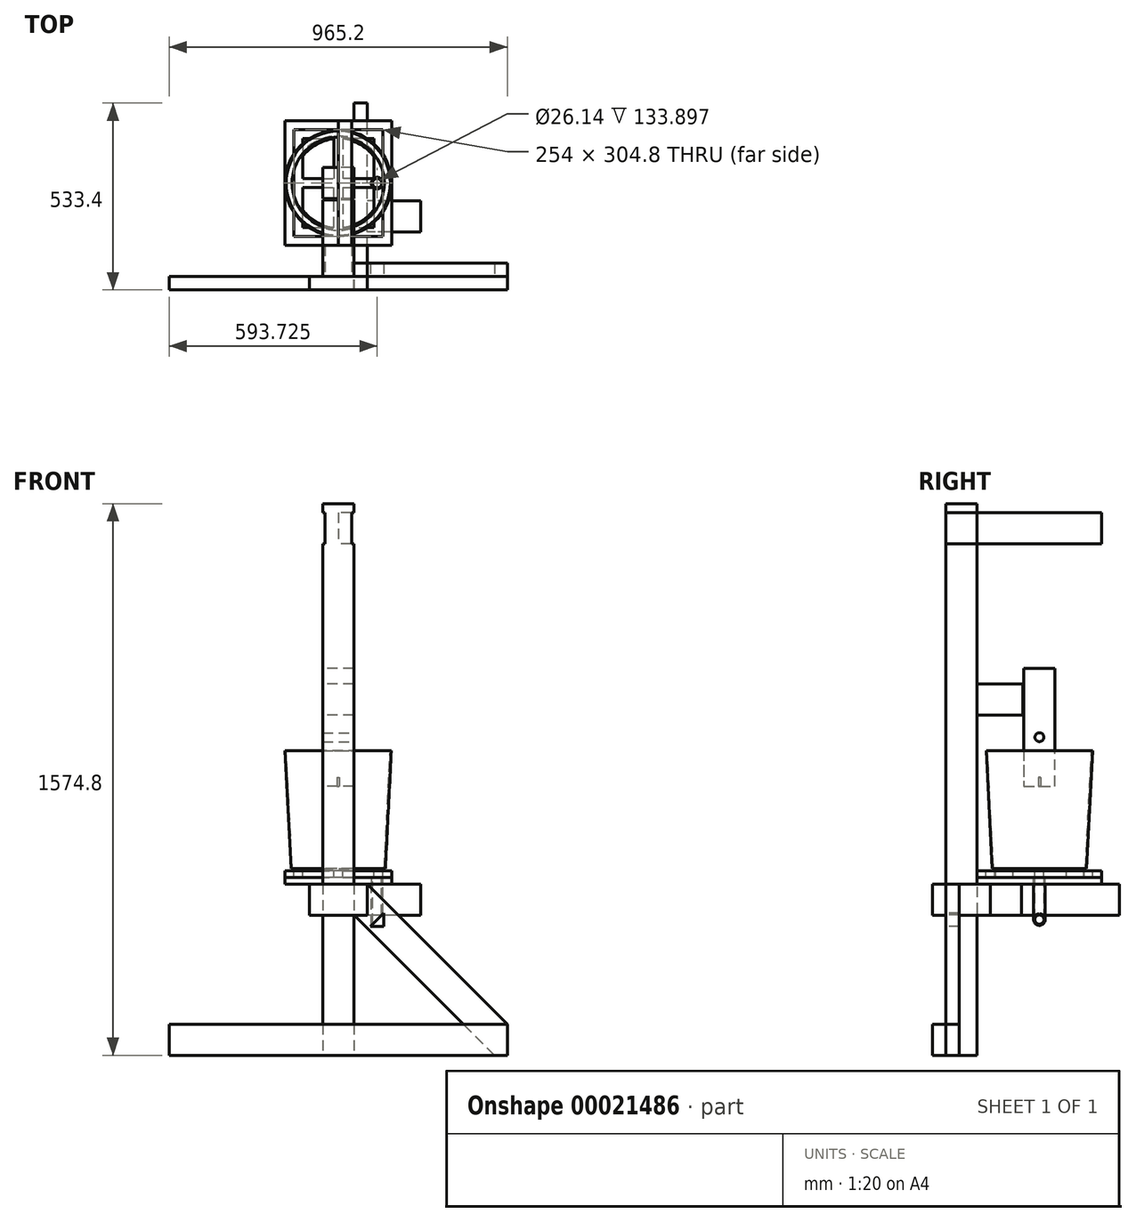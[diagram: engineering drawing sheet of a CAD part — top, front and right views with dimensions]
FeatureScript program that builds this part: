
annotation { "Feature Type Name" : "Feature", "Feature Type Description" : "" }
export const myFeature = defineFeature(function(context is Context, id is Id, definition is map)
    precondition{}
    {
        {
            var Q0;
            Q0=qCreatedBy(makeId("Front.planeOp"),FACE);
            var sketch = newSketch(context, id + "F0", { "sketchPlane" : qUnion([Q0])});
            skLineSegment(sketch, "E0", {"start": v(0, 0) * mm, "end": v(133.35, 0) * mm});
            skLineSegment(sketch, "E1", {"start": v(133.35, 0) * mm, "end": v(151.6, 361.95) * mm});
            skLineSegment(sketch, "E2", {"start": v(151.6, 361.95) * mm, "end": v(0, 361.95) * mm});
            skLineSegment(sketch, "E3", {"start": v(0, 361.95) * mm, "end": v(0, 0) * mm});
            skLineSegment(sketch, "E4", {"start": v(0, 0) * mm, "end": v(0, -74.22) * mm, "construction": true});
            skSolve(sketch);
        }
        {
            var Q0;
            Q0=qSketchRegion(id+"F0",true);
            var Q1;
            Q1=sQuery(id+"F0.wireOp",EDGE,"E4");
            revolve(context, id + "F1", {"entities" : qUnion([Q0]), "axis" : qUnion([Q1]), "revolveType" : RevolveType.FULL});
        }
        {
            var Q0;
            Q0=makeQuery(id+"F1.opRevolve","SWEPT_FACE",FACE,{"disambiguationData":[OSD([sQuery(id+"F0.wireOp",EDGE,"E2")])]});
            shell(context, id + "F2", {"entities" : qUnion([Q0]), "thickness" : 3.17 * mm});
        }
        {
            var Q0;
            Q0=qCreatedBy(makeId("Front.planeOp"),FACE);
            var sketch = newSketch(context, id + "F3", { "sketchPlane" : qUnion([Q0])});
            skLineSegment(sketch, "E5.bottom", {"start": v(-144.72, 25.4) * mm, "end": v(147.3, 25.4) * mm});
            skLineSegment(sketch, "E5.top", {"start": v(-144.72, -21.83) * mm, "end": v(147.3, -21.83) * mm});
            skLineSegment(sketch, "E5.left", {"start": v(-144.72, 25.4) * mm, "end": v(-144.72, -21.83) * mm});
            skLineSegment(sketch, "E5.right", {"start": v(147.3, 25.4) * mm, "end": v(147.3, -21.83) * mm});
            skSolve(sketch);
        }
        {
            var Q0;
            Q0=qSketchRegion(id+"F3",true);
            extrude(context, id + "F4", {"entities" : qUnion([Q0]), "operationType" : NewBodyOperationType.REMOVE, "endBound" : BoundingType.THROUGH_ALL, "depth" : 25.4 * mm, "hasSecondDirection" : true, "secondDirectionBound" : BoundingType.THROUGH_ALL, "secondDirectionOppositeDirection" : true, "secondDirectionDepth" : 25.4 * mm});
        }
        {
            var Q0;
            Q0=qCreatedBy(makeId("Top.planeOp"),FACE);
            var sketch = newSketch(context, id + "F5", { "sketchPlane" : qUnion([Q0])});
            skCircle(sketch, "E6", {"center": v(0, 0) * mm, "radius": 127 * mm});
            skSolve(sketch);
        }
        {
            var Q0;
            Q0=qSketchRegion(id+"F5",true);
            extrude(context, id + "F6", {"entities" : qUnion([Q0]), "depth" : 19.05 * mm});
        }
        {
            var Q0;
            Q0=qCreatedBy(makeId("Top.planeOp"),FACE);
            var sketch = newSketch(context, id + "F7", { "sketchPlane" : qUnion([Q0])});
            skLineSegment(sketch, "E7.rect.bottom", {"start": v(152.4, -177.8) * mm, "end": v(-152.4, -177.8) * mm});
            skLineSegment(sketch, "E7.rect.top", {"start": v(152.4, 177.8) * mm, "end": v(-152.4, 177.8) * mm});
            skLineSegment(sketch, "E7.rect.left", {"start": v(152.4, -177.8) * mm, "end": v(152.4, 177.8) * mm});
            skLineSegment(sketch, "E7.rect.right", {"start": v(-152.4, -177.8) * mm, "end": v(-152.4, 177.8) * mm});
            skPoint(sketch, "E7.rect.middle", {"position": v(0, 0) * mm});
            skCircle(sketch, "E8", {"center": v(111.13, 0) * mm, "radius": 15.88 * mm});
            skSolve(sketch);
        }
        {
            var Q0;
            Q0=qSketchRegion(id+"F7",true);
            extrude(context, id + "F8", {"entities" : qUnion([Q0]), "depth" : 19.05 * mm});
        }
        {
            var Q0;
            Q0=makeQuery(id+"F8.opExtrude","CAP_FACE",FACE,{"disambiguationData":[OSD([sQuery(id+"F7.wireOp",EDGE,"E7.rect.bottom"),sQuery(id+"F7.wireOp",EDGE,"E7.rect.top"),sQuery(id+"F7.wireOp",EDGE,"E7.rect.left"),sQuery(id+"F7.wireOp",EDGE,"E7.rect.right")])],"isStart":true});
            extrude(context, id + "F9", {"entities" : qUnion([Q0]), "depth" : 19.05 * mm});
        }
        {
            var Q0;
            Q0=makeQuery(id+"F8.opExtrude","CAP_FACE",FACE,{"disambiguationData":[OSD([sQuery(id+"F7.wireOp",EDGE,"E7.rect.bottom"),sQuery(id+"F7.wireOp",EDGE,"E7.rect.top"),sQuery(id+"F7.wireOp",EDGE,"E7.rect.left"),sQuery(id+"F7.wireOp",EDGE,"E7.rect.right")])],"isStart":false});
            var sketch = newSketch(context, id + "F10", { "sketchPlane" : qUnion([Q0])});
            skLineSegment(sketch, "E9.rect.bottom", {"start": v(127, 152.4) * mm, "end": v(-127, 152.4) * mm});
            skLineSegment(sketch, "E9.rect.top", {"start": v(127, -152.4) * mm, "end": v(-127, -152.4) * mm});
            skLineSegment(sketch, "E9.rect.left", {"start": v(127, 152.4) * mm, "end": v(127, -152.4) * mm});
            skLineSegment(sketch, "E9.rect.right", {"start": v(-127, 152.4) * mm, "end": v(-127, -152.4) * mm});
            skLineSegment(sketch, "E10.bottom", {"start": v(-101.6, 127) * mm, "end": v(-12.7, 127) * mm});
            skLineSegment(sketch, "E10.top", {"start": v(-101.6, 12.7) * mm, "end": v(-12.7, 12.7) * mm});
            skLineSegment(sketch, "E10.left", {"start": v(-101.6, 127) * mm, "end": v(-101.6, 12.7) * mm});
            skLineSegment(sketch, "E10.right", {"start": v(-12.7, 127) * mm, "end": v(-12.7, 12.7) * mm});
            skLineSegment(sketch, "E11.bottom", {"start": v(101.6, 127) * mm, "end": v(12.7, 127) * mm});
            skLineSegment(sketch, "E11.top", {"start": v(101.6, 12.7) * mm, "end": v(12.7, 12.7) * mm});
            skLineSegment(sketch, "E11.left", {"start": v(101.6, 127) * mm, "end": v(101.6, 12.7) * mm});
            skLineSegment(sketch, "E11.right", {"start": v(12.7, 127) * mm, "end": v(12.7, 12.7) * mm});
            skLineSegment(sketch, "E12.bottom", {"start": v(-101.6, -127) * mm, "end": v(-12.7, -127) * mm});
            skLineSegment(sketch, "E12.top", {"start": v(-101.6, -12.7) * mm, "end": v(-12.7, -12.7) * mm});
            skLineSegment(sketch, "E12.left", {"start": v(-101.6, -127) * mm, "end": v(-101.6, -12.7) * mm});
            skLineSegment(sketch, "E12.right", {"start": v(-12.7, -127) * mm, "end": v(-12.7, -12.7) * mm});
            skLineSegment(sketch, "E13.bottom", {"start": v(12.7, -12.7) * mm, "end": v(101.6, -12.7) * mm});
            skLineSegment(sketch, "E13.top", {"start": v(12.7, -127) * mm, "end": v(101.6, -127) * mm});
            skLineSegment(sketch, "E13.left", {"start": v(12.7, -12.7) * mm, "end": v(12.7, -127) * mm});
            skLineSegment(sketch, "E13.right", {"start": v(101.6, -12.7) * mm, "end": v(101.6, -127) * mm});
            skSolve(sketch);
        }
        {
            var Q0;
            Q0=qSketchRegion(id+"F10",true);
            extrude(context, id + "F11", {"entities" : qUnion([Q0]), "operationType" : NewBodyOperationType.REMOVE, "oppositeDirection" : true, "depth" : 19.05 * mm});
        }
        {
            var Q0;
            Q0=makeQuery(id+"F9.opExtrude","CAP_FACE",FACE,{"disambiguationData":[OSD([sQuery(id+"F7.wireOp",EDGE,"E7.rect.bottom"),sQuery(id+"F7.wireOp",EDGE,"E7.rect.top"),sQuery(id+"F7.wireOp",EDGE,"E7.rect.left"),sQuery(id+"F7.wireOp",EDGE,"E7.rect.right"),sQuery(id+"F7.wireOp",EDGE,"E8")])],"isStart":false});
            var sketch = newSketch(context, id + "F12", { "sketchPlane" : qUnion([Q0])});
            skLineSegment(sketch, "E14.bottom", {"start": v(44.45, 228.6) * mm, "end": v(82.55, 228.6) * mm});
            skLineSegment(sketch, "E14.top", {"start": v(44.45, -228.6) * mm, "end": v(82.55, -228.6) * mm});
            skLineSegment(sketch, "E14.left", {"start": v(44.45, 228.6) * mm, "end": v(44.45, -228.6) * mm});
            skLineSegment(sketch, "E14.right", {"start": v(82.55, 228.6) * mm, "end": v(82.55, -228.6) * mm});
            skSolve(sketch);
        }
        {
            var Q0;
            Q0=qSketchRegion(id+"F12",true);
            extrude(context, id + "F13", {"entities" : qUnion([Q0]), "depth" : 88.9 * mm});
        }
        {
            var Q0;
            Q0=qCreatedBy(makeId("Top.planeOp"),FACE);
            var sketch = newSketch(context, id + "F14", { "sketchPlane" : qUnion([Q0])});
            skLineSegment(sketch, "E15.bottom", {"start": v(44.45, -266.7) * mm, "end": v(-44.45, -266.7) * mm});
            skLineSegment(sketch, "E15.top", {"start": v(44.45, -177.8) * mm, "end": v(-44.45, -177.8) * mm});
            skLineSegment(sketch, "E15.left", {"start": v(44.45, -266.7) * mm, "end": v(44.45, -177.8) * mm});
            skLineSegment(sketch, "E15.right", {"start": v(-44.45, -266.7) * mm, "end": v(-44.45, -177.8) * mm});
            skSolve(sketch);
        }
        {
            var Q0;
            Q0=qSketchRegion(id+"F14",true);
            extrude(context, id + "F15", {"entities" : qUnion([Q0]), "depth" : 1066.8 * mm, "hasSecondDirection" : true, "secondDirectionOppositeDirection" : true, "secondDirectionDepth" : 508 * mm});
        }
        {
            var Q0;
            Q0=makeQuery(id+"F15.opExtrude","SWEPT_FACE",FACE,{"disambiguationData":[OSD([sQuery(id+"F14.wireOp",EDGE,"E15.bottom")])]});
            var sketch = newSketch(context, id + "F16", { "sketchPlane" : qUnion([Q0])});
            skLineSegment(sketch, "E16.bottom", {"start": v(-482.6, -508) * mm, "end": v(482.6, -508) * mm});
            skLineSegment(sketch, "E16.top", {"start": v(-482.6, -419.1) * mm, "end": v(482.6, -419.1) * mm});
            skLineSegment(sketch, "E16.left", {"start": v(-482.6, -508) * mm, "end": v(-482.6, -419.1) * mm});
            skLineSegment(sketch, "E16.right", {"start": v(482.6, -508) * mm, "end": v(482.6, -419.1) * mm});
            skLineSegment(sketch, "E17", {"start": v(445.78, -508) * mm, "end": v(44.45, -106.67) * mm});
            skLineSegment(sketch, "E18", {"start": v(44.45, -106.67) * mm, "end": v(44.45, -19.05) * mm});
            skLineSegment(sketch, "E19", {"start": v(82.55, -19.05) * mm, "end": v(482.6, -419.1) * mm});
            skLineSegment(sketch, "E20", {"start": v(82.55, -19.05) * mm, "end": v(44.45, -19.05) * mm});
            skLineSegment(sketch, "E21", {"start": v(0, -508) * mm, "end": v(0, -702.08) * mm, "construction": true});
            skLineSegment(sketch, "E22", {"start": v(44.45, -19.05) * mm, "end": v(-82.55, -19.05) * mm});
            skLineSegment(sketch, "E23", {"start": v(-82.55, -19.05) * mm, "end": v(-82.55, -107.95) * mm});
            skLineSegment(sketch, "E24", {"start": v(-82.55, -107.95) * mm, "end": v(82.55, -107.95) * mm});
            skLineSegment(sketch, "E25", {"start": v(82.55, -107.95) * mm, "end": v(82.55, -19.05) * mm});
            skSolve(sketch);
        }
        {
            var Q0;
            {var subQ1=sQuery(id+"F16.wireOp",EDGE,"E18");Q0=makeQuery(id+"F16.imprint","IMPRINT",FACE,{"disambiguationData":[TD([[makeQuery(id+"F16.imprint","IMPRINT",EDGE,{"derivedFrom":subQ1}),1.0]])]});}
            var Q1;
            {var subQ5=sQuery(id+"F16.wireOp",EDGE,"E16.right");Q1=makeQuery(id+"F16.imprint","IMPRINT",FACE,{"disambiguationData":[TD([[makeQuery(id+"F16.imprint","IMPRINT",EDGE,{"derivedFrom":subQ5}),1.0]])]});}
            var Q2;
            {var subQ4=sQuery(id+"F16.wireOp",EDGE,"E19");Q2=makeQuery(id+"F16.imprint","IMPRINT",FACE,{"disambiguationData":[TD([[makeQuery(id+"F16.imprint","IMPRINT",EDGE,{"derivedFrom":subQ4}),-1.0]])]});}
            extrude(context, id + "F17", {"entities" : qUnion([Q0, Q1, Q2]), "oppositeDirection" : true, "depth" : 38.1 * mm});
        }
        {
            var Q0;
            {var subQ5=sQuery(id+"F16.wireOp",EDGE,"E16.left");Q0=makeQuery(id+"F16.imprint","IMPRINT",FACE,{"disambiguationData":[TD([[makeQuery(id+"F16.imprint","IMPRINT",EDGE,{"derivedFrom":subQ5}),-1.0]])]});}
            var Q1;
            {var subQ0=sQuery(id+"F14.wireOp",EDGE,"E15.bottom");var subQ1=makeQuery(id+"F15.opExtrude","SWEPT_EDGE",EDGE,{"disambiguationData":[OSD([subQ0,sQuery(id+"F14.wireOp",EDGE,"E15.right")])]});var subQ4=sQuery(id+"F16.wireOp",EDGE,"E16.bottom");var subQ5=makeQuery(id+"F16.imprint","INTERSECT",VERTEX,{"derivedFrom":[subQ1,subQ4]});var subQ6=makeQuery(id+"F15.opExtrude","SWEPT_EDGE",EDGE,{"disambiguationData":[OSD([subQ0,sQuery(id+"F14.wireOp",EDGE,"E15.left")])]});var subQ8=makeQuery(id+"F16.imprint","INTERSECT",VERTEX,{"derivedFrom":[subQ6,subQ4]});Q1=makeQuery(id+"F16.imprint","IMPRINT",FACE,{"disambiguationData":[TD([[makeQuery(id+"F16.imprint","IMPRINT",EDGE,{"disambiguationData":[TD([[subQ8,-1.0],[subQ5,1.0]])],"derivedFrom":subQ4}),-1.0]])]});}
            var Q2;
            {var subQ3=sQuery(id+"F16.wireOp",EDGE,"E16.bottom");var subQ5=sQuery(id+"F16.wireOp",EDGE,"E17");var subQ7=makeQuery(id+"F16.imprint","INTERSECT",VERTEX,{"derivedFrom":[subQ3,subQ5]});Q2=makeQuery(id+"F16.imprint","IMPRINT",FACE,{"disambiguationData":[TD([[makeQuery(id+"F16.imprint","IMPRINT",EDGE,{"disambiguationData":[TD([[subQ7,-1.0]])],"derivedFrom":subQ5}),1.0]])]});}
            var Q3;
            {var subQ5=sQuery(id+"F16.wireOp",EDGE,"E16.right");Q3=makeQuery(id+"F16.imprint","IMPRINT",FACE,{"disambiguationData":[TD([[makeQuery(id+"F16.imprint","IMPRINT",EDGE,{"derivedFrom":subQ5}),1.0]])]});}
            var Q4;
            {var subQ5=sQuery(id+"F16.wireOp",EDGE,"E23");Q4=makeQuery(id+"F16.imprint","IMPRINT",FACE,{"disambiguationData":[TD([[makeQuery(id+"F16.imprint","IMPRINT",EDGE,{"derivedFrom":subQ5}),1.0]])]});}
            var Q5;
            {var subQ8=sQuery(id+"F16.wireOp",EDGE,"E18");Q5=makeQuery(id+"F16.imprint","IMPRINT",FACE,{"disambiguationData":[TD([[makeQuery(id+"F16.imprint","IMPRINT",EDGE,{"derivedFrom":subQ8}),-1.0]])]});}
            var Q6;
            {var subQ4=sQuery(id+"F16.wireOp",EDGE,"E18");Q6=makeQuery(id+"F16.imprint","IMPRINT",FACE,{"disambiguationData":[TD([[makeQuery(id+"F16.imprint","IMPRINT",EDGE,{"derivedFrom":subQ4}),1.0]])]});}
            extrude(context, id + "F18", {"entities" : qUnion([Q0, Q1, Q2, Q3, Q4, Q5, Q6]), "depth" : 38.1 * mm});
        }
        {
            var Q0;
            Q0=qCreatedBy(makeId("Right.planeOp"),FACE);
            var sketch = newSketch(context, id + "F19", { "sketchPlane" : qUnion([Q0])});
            skLineSegment(sketch, "E26.bottom", {"start": v(-177.8, 1041.4) * mm, "end": v(177.8, 1041.4) * mm});
            skLineSegment(sketch, "E26.top", {"start": v(-177.8, 952.5) * mm, "end": v(177.8, 952.5) * mm});
            skLineSegment(sketch, "E26.left", {"start": v(-177.8, 1041.4) * mm, "end": v(-177.8, 952.5) * mm});
            skLineSegment(sketch, "E26.right", {"start": v(177.8, 1041.4) * mm, "end": v(177.8, 952.5) * mm});
            skLineSegment(sketch, "E27", {"start": v(0, 0) * mm, "end": v(0, 1223.4) * mm, "construction": true});
            skSolve(sketch);
        }
        {
            var Q0;
            Q0=qSketchRegion(id+"F19",true);
            extrude(context, id + "F20", {"entities" : qUnion([Q0]), "depth" : 38.1 * mm});
        }
        {
            var Q0;
            Q0=makeQuery(id+"F20.opExtrude","CAP_FACE",FACE,{"disambiguationData":[OSD([sQuery(id+"F19.wireOp",EDGE,"E26.bottom"),sQuery(id+"F19.wireOp",EDGE,"E26.top"),sQuery(id+"F19.wireOp",EDGE,"E26.left"),sQuery(id+"F19.wireOp",EDGE,"E26.right")])],"isStart":false});
            var sketch = newSketch(context, id + "F21", { "sketchPlane" : qUnion([Q0])});
            skLineSegment(sketch, "E28", {"start": v(-177.8, 1041.4) * mm, "end": v(177.8, 952.5) * mm, "construction": true});
            skLineSegment(sketch, "E29.rect.bottom", {"start": v(266.7, 952.5) * mm, "end": v(-266.7, 952.5) * mm});
            skLineSegment(sketch, "E29.rect.top", {"start": v(266.7, 1041.4) * mm, "end": v(-266.7, 1041.4) * mm});
            skLineSegment(sketch, "E29.rect.left", {"start": v(266.7, 952.5) * mm, "end": v(266.7, 1041.4) * mm});
            skLineSegment(sketch, "E29.rect.right", {"start": v(-266.7, 952.5) * mm, "end": v(-266.7, 1041.4) * mm});
            skPoint(sketch, "E29.rect.middle", {"position": v(0, 996.95) * mm});
            skSolve(sketch);
        }
        {
            var Q0;
            Q0=qSketchRegion(id+"F21",true);
            extrude(context, id + "F22", {"entities" : qUnion([Q0]), "depth" : 38.1 * mm});
        }
        {
            var Q0;
            Q0=makeQuery(id+"F15.opExtrude","SWEPT_FACE",FACE,{"disambiguationData":[OSD([sQuery(id+"F14.wireOp",EDGE,"E15.bottom")])]});
            var sketch = newSketch(context, id + "F23", { "sketchPlane" : qUnion([Q0])});
            skLineSegment(sketch, "E30.bottom", {"start": v(38.1, 1041.4) * mm, "end": v(76.2, 1041.4) * mm});
            skLineSegment(sketch, "E30.top", {"start": v(38.1, 952.5) * mm, "end": v(76.2, 952.5) * mm});
            skLineSegment(sketch, "E30.left", {"start": v(38.1, 1041.4) * mm, "end": v(38.1, 952.5) * mm});
            skLineSegment(sketch, "E30.right", {"start": v(76.2, 1041.4) * mm, "end": v(76.2, 952.5) * mm});
            skLineSegment(sketch, "E31.bottom", {"start": v(-38.1, 1041.4) * mm, "end": v(-76.2, 1041.4) * mm});
            skLineSegment(sketch, "E31.top", {"start": v(-38.1, 952.5) * mm, "end": v(-76.2, 952.5) * mm});
            skLineSegment(sketch, "E31.left", {"start": v(-38.1, 1041.4) * mm, "end": v(-38.1, 952.5) * mm});
            skLineSegment(sketch, "E31.right", {"start": v(-76.2, 1041.4) * mm, "end": v(-76.2, 952.5) * mm});
            skLineSegment(sketch, "E32", {"start": v(0, 1066.8) * mm, "end": v(0, 856.9) * mm, "construction": true});
            skSolve(sketch);
        }
        {
            var Q0;
            Q0=qSketchRegion(id+"F23",true);
            extrude(context, id + "F24", {"entities" : qUnion([Q0]), "operationType" : NewBodyOperationType.REMOVE, "endBound" : BoundingType.THROUGH_ALL, "oppositeDirection" : true, "depth" : 25.4 * mm});
        }
        {
            var Q0;
            Q0=qCreatedBy(makeId("Right.planeOp"),FACE);
            var sketch = newSketch(context, id + "F25", { "sketchPlane" : qUnion([Q0])});
            skLineSegment(sketch, "E33.bottom", {"start": v(-177.8, 552.45) * mm, "end": v(-47.63, 552.45) * mm});
            skLineSegment(sketch, "E33.top", {"start": v(-177.8, 463.55) * mm, "end": v(-47.63, 463.55) * mm});
            skLineSegment(sketch, "E33.left", {"start": v(-177.8, 552.45) * mm, "end": v(-177.8, 463.55) * mm});
            skLineSegment(sketch, "E33.right", {"start": v(-47.63, 552.45) * mm, "end": v(-47.63, 463.55) * mm});
            skLineSegment(sketch, "E34", {"start": v(0, 0) * mm, "end": v(0, 816.17) * mm, "construction": true});
            skSolve(sketch);
        }
        {
            var Q0;
            Q0=qSketchRegion(id+"F25",true);
            extrude(context, id + "F26", {"entities" : qUnion([Q0]), "depth" : 88.9 * mm, "symmetric" : true});
        }
        {
            var Q0;
            Q0=qCreatedBy(makeId("Right.planeOp"),FACE);
            var sketch = newSketch(context, id + "F27", { "sketchPlane" : qUnion([Q0])});
            skLineSegment(sketch, "E35.bottom", {"start": v(-50.8, 977.9) * mm, "end": v(50.8, 977.9) * mm, "construction": true});
            skLineSegment(sketch, "E35.top", {"start": v(-44.45, 596.9) * mm, "end": v(44.45, 596.9) * mm});
            skLineSegment(sketch, "E35.left", {"start": v(-50.8, 977.9) * mm, "end": v(-50.8, 596.9) * mm, "construction": true});
            skLineSegment(sketch, "E35.right", {"start": v(50.8, 977.9) * mm, "end": v(50.8, 596.9) * mm, "construction": true});
            skLineSegment(sketch, "E36", {"start": v(-50.8, 790.58) * mm, "end": v(50.8, 790.58) * mm, "construction": true});
            skPoint(sketch, "E37", {"position": v(0, 596.9) * mm});
            skLineSegment(sketch, "E38", {"start": v(-44.45, 596.9) * mm, "end": v(-44.45, 260.35) * mm});
            skLineSegment(sketch, "E39", {"start": v(-44.45, 260.35) * mm, "end": v(44.45, 260.35) * mm});
            skLineSegment(sketch, "E40", {"start": v(44.45, 260.35) * mm, "end": v(44.45, 596.9) * mm});
            skPoint(sketch, "E41", {"position": v(0, 260.35) * mm});
            skLineSegment(sketch, "E42", {"start": v(-50.8, 596.9) * mm, "end": v(-44.45, 596.9) * mm});
            skLineSegment(sketch, "E43", {"start": v(44.45, 596.9) * mm, "end": v(50.8, 596.9) * mm});
            skSolve(sketch);
        }
        {
            var Q0;
            Q0=qSketchRegion(id+"F27",true);
            extrude(context, id + "F28", {"entities" : qUnion([Q0]), "depth" : 88.9 * mm, "symmetric" : true});
        }
        {
            var Q0;
            Q0=makeQuery(id+"F28.opExtrude","SWEPT_FACE",FACE,{"disambiguationData":[OSD([sQuery(id+"F27.wireOp",EDGE,"E39")])]});
            var sketch = newSketch(context, id + "F29", { "sketchPlane" : qUnion([Q0])});
            skCircle(sketch, "E44", {"center": v(0, 0) * mm, "radius": 3.18 * mm});
            skSolve(sketch);
        }
        {
            var Q0;
            Q0=makeQuery(id+"F29.imprint","IMPRINT",FACE,{"disambiguationData":[TD([[makeQuery(id+"F29.imprint","IMPRINT",EDGE,{"derivedFrom":sQuery(id+"F29.wireOp",EDGE,"E44")}),1.0]])]});
            extrude(context, id + "F30", {"entities" : qUnion([Q0]), "operationType" : NewBodyOperationType.REMOVE, "oppositeDirection" : true, "depth" : 25.4 * mm});
        }
        {
            var Q0;
            Q0=makeQuery(id+"F28.opExtrude","CAP_FACE",FACE,{"disambiguationData":[OSD([sQuery(id+"F27.wireOp",EDGE,"E35.top"),sQuery(id+"F27.wireOp",EDGE,"E38"),sQuery(id+"F27.wireOp",EDGE,"E39"),sQuery(id+"F27.wireOp",EDGE,"E40")])],"isStart":false});
            var sketch = newSketch(context, id + "F31", { "sketchPlane" : qUnion([Q0])});
            skCircle(sketch, "E45", {"center": v(0, 400.05) * mm, "radius": 12.7 * mm});
            skPoint(sketch, "E46", {"position": v(0, 260.35) * mm});
            skSolve(sketch);
        }
        {
            var Q0;
            Q0=qSketchRegion(id+"F31",true);
            extrude(context, id + "F32", {"entities" : qUnion([Q0]), "operationType" : NewBodyOperationType.REMOVE, "endBound" : BoundingType.THROUGH_ALL, "oppositeDirection" : true, "depth" : 25.4 * mm});
        }
        {
            var Q0;
            Q0=makeQuery(id+"F9.opExtrude","CAP_FACE",FACE,{"disambiguationData":[OSD([sQuery(id+"F7.wireOp",EDGE,"E7.rect.bottom"),sQuery(id+"F7.wireOp",EDGE,"E7.rect.top"),sQuery(id+"F7.wireOp",EDGE,"E7.rect.left"),sQuery(id+"F7.wireOp",EDGE,"E7.rect.right"),sQuery(id+"F7.wireOp",EDGE,"E8")])],"isStart":true});
            var sketch = newSketch(context, id + "F33", { "sketchPlane" : qUnion([Q0])});
            skCircle(sketch, "E47", {"center": v(111.13, 0) * mm, "radius": 16.7 * mm});
            skCircle(sketch, "E48", {"center": v(111.13, 0) * mm, "radius": 13.07 * mm});
            skSolve(sketch);
        }
        {
            var Q0;
            Q0 = qSketchRegion(id + "F33", true);
            extrude(context, id + "F34", {"entities" : qUnion([Q0]), "oppositeDirection" : true, "depth" : 139.7 * mm});
        }
        {
            var Q0;
            Q0=qCreatedBy(makeId("Front.planeOp"),FACE);
            var sketch = newSketch(context, id + "F35", { "sketchPlane" : qUnion([Q0])});
            skLineSegment(sketch, "E49", {"start": v(92.08, -139.7) * mm, "end": v(130.18, -101.6) * mm});
            skLineSegment(sketch, "E50", {"start": v(130.18, -101.6) * mm, "end": v(130.18, -139.7) * mm});
            skLineSegment(sketch, "E51", {"start": v(130.18, -139.7) * mm, "end": v(92.08, -139.7) * mm});
            skPoint(sketch, "E52", {"position": v(111.13, -139.7) * mm});
            skSolve(sketch);
        }
        {
            var Q0;
            Q0 = qSketchRegion(id + "F35", true);
            extrude(context, id + "F36", {"entities" : qUnion([Q0]), "operationType" : NewBodyOperationType.REMOVE, "endBound" : BoundingType.THROUGH_ALL, "oppositeDirection" : true, "depth" : 25.4 * mm, "hasSecondDirection" : true, "secondDirectionBound" : BoundingType.THROUGH_ALL, "secondDirectionOppositeDirection" : false, "secondDirectionDepth" : 25.4 * mm});
        }
        {
            var Q0;
            Q0=makeQuery(id+"F13.opExtrude","SWEPT_FACE",FACE,{"disambiguationData":[OSD([sQuery(id+"F12.wireOp",EDGE,"E14.right")])]});
            var sketch = newSketch(context, id + "F37", { "sketchPlane" : qUnion([Q0])});
            skLineSegment(sketch, "E53.bottom", {"start": v(-139.7, -107.95) * mm, "end": v(-50.8, -107.95) * mm});
            skLineSegment(sketch, "E53.top", {"start": v(-139.7, -19.05) * mm, "end": v(-50.8, -19.05) * mm});
            skLineSegment(sketch, "E53.left", {"start": v(-139.7, -107.95) * mm, "end": v(-139.7, -19.05) * mm});
            skLineSegment(sketch, "E53.right", {"start": v(-50.8, -107.95) * mm, "end": v(-50.8, -19.05) * mm});
            skSolve(sketch);
        }
        {
            var Q0;
            Q0 = qSketchRegion(id + "F37", true);
            extrude(context, id + "F38", {"entities" : qUnion([Q0]), "depth" : 152.4 * mm});
        }
    });
